# Revit family: DUA-DAM-AEC-Fire_Damper
name_source: partatom
category: Duct Accessories
revit_build: Autodesk Revit 2016 (Build: 20150220_1215(x64)
units: mm (PartAtom-declared; Revit-internal decimal feet)

## family parameters
Always vertical = Yes
Cut with Voids When Loaded = No
OmniClass Number = 23.60.70.11.11
OmniClass Title = Fire Dampers
Part Type = Damper
Round Connector Dimension = Use Diameter
Shared = No
Work Plane-Based = No

## types (1)
- Standard
    Blade Material = Steel, Mild
    Blade Number = 2
    Blade Offset = 250 mm  [stored 0.82021 ft]
    Depth = 200 mm  [stored 0.656168 ft]
    Frame Material = Steel, Mild
    Frame Thickness = 50 mm  [stored 0.164042 ft]
    Height = 600 mm
    Internal Height = 500 mm  [stored 1.64042 ft]
    Internal Width = 500 mm  [stored 1.64042 ft]
    Large Enough = No
    Width = 600 mm

note: [stored X ft] marks values corroborated as IEEE doubles in the binary element streams (Revit-internal decimal feet)

## geometry (parser evidence)
native form markers: Blend x2, Sweep x7
no freeform markers — native parametric forms only
